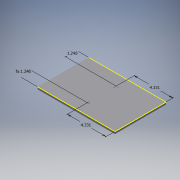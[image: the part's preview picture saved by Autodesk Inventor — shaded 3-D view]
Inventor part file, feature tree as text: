
AUTODESK INVENTOR PART (.ipt)
format: ipt  version: 2019 (Build 230136000, 136)  size: 101,888 bytes
history: native  units: in
note: dims shown in document units (in); Inventor stores cm internally (conversion verified against a paired STEP export)
features: sketch x2, extrude x1
ambient origin geometry x8: Origin, YZ Plane, XZ Plane, XY Plane, X Axis, Y Axis, Z Axis, Center Point
bodies: Solid1 (feature_tree)
feature tree (3):
  extrude  "Extrusion1"  Depth=5.7087in
  sketch  "Sketch4"  dims[d2=0.25in d3=0.0in d24=1.2402in d25=1.2402in d26=4.3307in d27=4.3307in]
  sketch  "Sketch1"  dims[d0=8.6614in d1=5.7087in]
